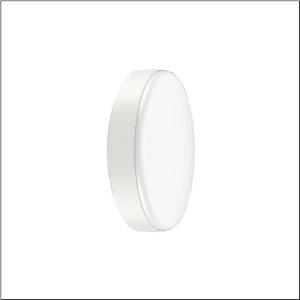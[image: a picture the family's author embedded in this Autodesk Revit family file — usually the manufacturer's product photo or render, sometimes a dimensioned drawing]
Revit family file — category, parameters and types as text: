
# Revit family: round_31_51wc10db34a
name_source: partatom
category: Lighting Fixtures
units: mm (PartAtom-declared; Revit-internal decimal feet)

## family parameters
Cut with Voids When Loaded = No
Host = Face
Light Source = No
Part Type = Normal
Room Calculation Point = No
Round Connector Dimension = Use Diameter
Shared = No

## types (1)
- Round 31 (1 x LED, 4250 lm, 34 W, 3000K)
    Apparent Load = 34 VA
    CIE Flux Codes = 44 75 94 94 100
    Color Rendering = 80
    Color Temperature = 3000K
    Default Elevation = 1800 mm
    Description = Round 31, wall and ceiling luminaire, primary optical cover: cover, of PC, opal, light emission: direct distribution, primary light characteristic: symmetric, installation type: surface-mounted, LED, rated luminous flux: 4.250lm, luminous efficacy: 125lm/W, light colour: 830, colour temperature: 3000K, control gear: DALI 2, with terminal, 5-pole, max. 2.5mm², mains connection: 220..240V, AC, 50/60Hz, rated input power: 34W, luminaire housing, of PC, traffic white (RAL 9016), diameter: 480mm, protection rating (complete): IP65, insulation class (complete): insulation class II (safety insulation), certification: CE, impact resistance: IK10, permissible operating ambient temperature: -20..+40°C, permissible storage temperature: -20..+60°C, packaging unit: 1 piece
    Height = 97 mm
    Lamp = 1 x LED
    Lamp Light Flux = 4250 lm
    Lamp Power = 34 W
    Lamp count = 1
    Length = 480 mm
    Luminous efficacy = 125 lm/W
    Manufacturer = Siteco
    ModVariant = No
    Model = 51WC10DB34A
    Mounting Place = Wall
    Mounting Type = Surface mounted
    Number of Poles = 1
    OnlyDefault = Yes
    Power Factor = 1
    Product Name = Round 31
    Product group = wall and ceiling luminaire
    ProductGroupID = 2001
    Protection Class = Protection class II
    Protection Degree = IP 65
    RLX_Detail_Level = 1
    RLX_Emergency_Light_Flux = 0 lm
    RLX_Emergency_Type = 0
    RLX_Emergency_Type_DB = No
    RlxData = <blob elided: 55313 chars, md5=08807cec>
    Socket = socket
    Standby Power = 0 W
    System Light Flux = 4250 lm
    System Power = 34 W
    Type Comments = Product without accessories
    Type Image = l_1007188.jpg
    URL = http://relux.com
    VarID = ---
    Voltage = 0 V
    Weight = 0.00 kg
    Width = 0 mm  [stored 0 ft]

note: [stored X ft] marks values corroborated as IEEE doubles in the binary element streams (Revit-internal decimal feet)

## geometry (parser evidence)
native form markers: Blend x4, Sweep x14
no freeform markers — native parametric forms only
